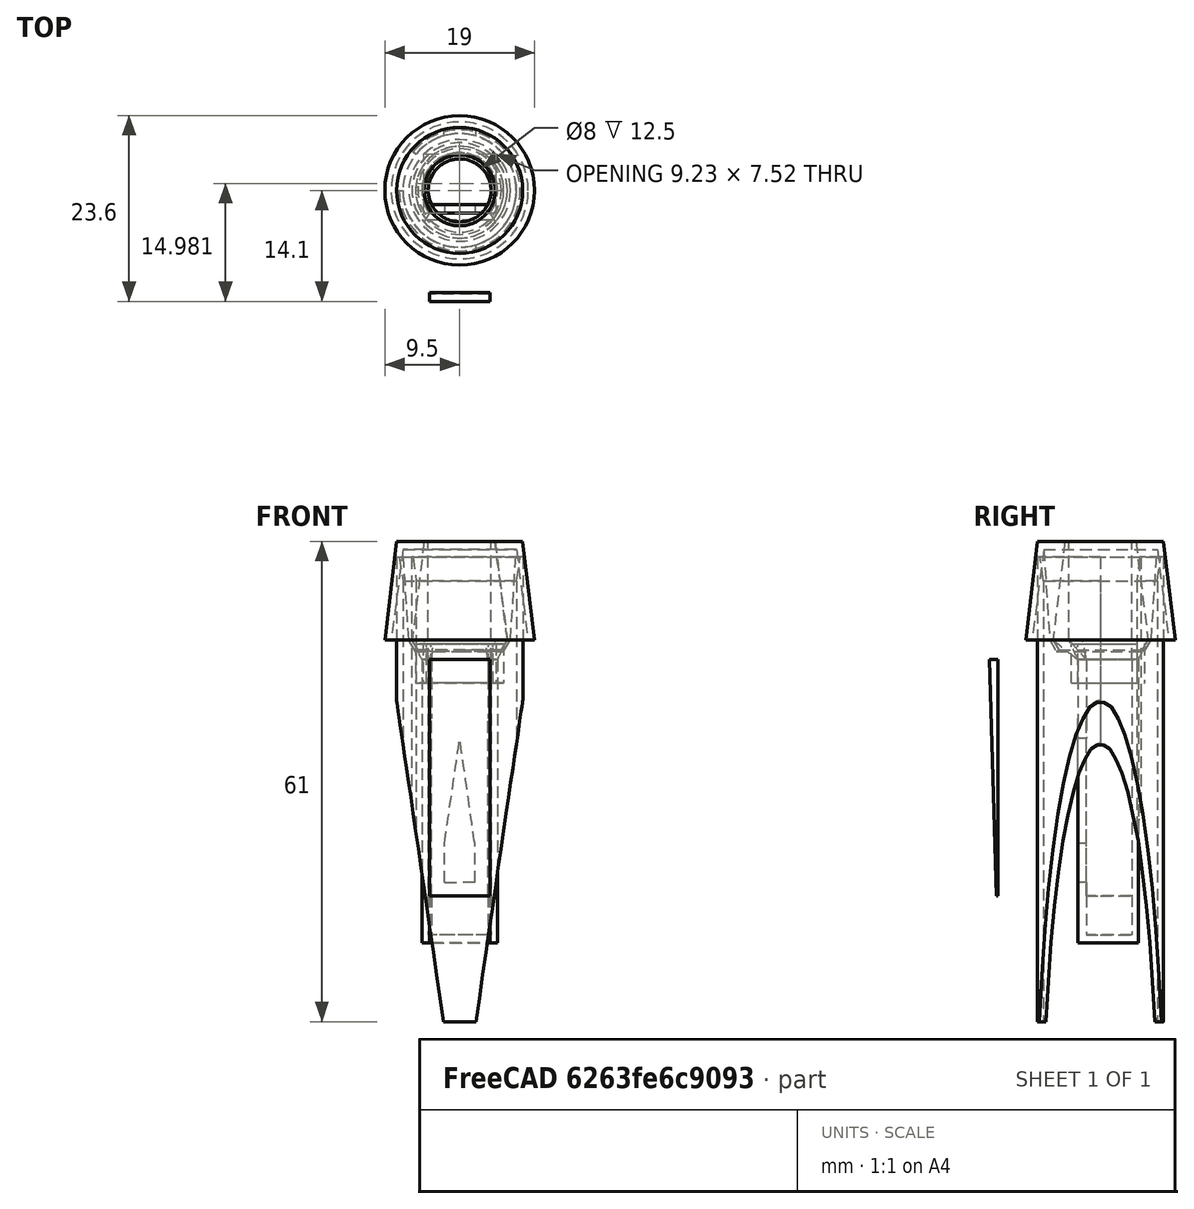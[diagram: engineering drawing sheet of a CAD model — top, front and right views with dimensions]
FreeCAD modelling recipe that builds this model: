
FCSTD DOCUMENT  (FreeCAD 1.1R44227 +647 (Git))
Label: stroik
License: All rights reserved
LicenseURL: https://en.wikipedia.org/wiki/All_rights_reserved
objects: Sketcher::SketchObject×15, PartDesign::Body×6, App::Point×6, PartDesign::Pocket×5, PartDesign::SubShapeBinder×5, PartDesign::Pad×4, PartDesign::AdditiveCylinder×2, PartDesign::Revolution×2, App::VarSet×1, PartDesign::Boolean×1, PartDesign::AdditiveLoft×1, Mesh::Feature×1
note: 85 computed .brp shape members not serialized (recipe doc carries the construction recipe); baked Part::Feature solids carry a one-line shape summary decoded from their .brp

FEATURE [App::VarSet] VarSet
  d_inner = 4
  d_outer = 4.8
  d_outer_plug = 6.05
  leaf_end_thickness = 0.2
  leaf_gap = 0
  leaf_len = 30
  leaf_start_thickness = 1.1
  plug_inner_start = 4
  plug_len = 15
  plug_outer_start = 4.5
FEATURE [PartDesign::AdditiveCylinder] Cylinder  label="HasCylinder"
  Angle = 360
  AttacherType = Attacher::AttachEngine3D
  FirstAngle = 0
  Height = 30
  Radius = 4.8
  Refine = true
  SecondAngle = 0
  Suppressed = false
  expr: Height = VarSet.leaf_len
  expr: Radius = VarSet.d_outer
FEATURE [Sketcher::SketchObject] Sketch
  ArcFitTolerance = 1e-06
  AttachmentSupport = -> [YZ_Plane]
  ExternalGeometry = -> [Cylinder]
  ExternalTypes = [0]
  FullyConstrained = true
  MakeInternals = false
  MapMode = 5
  Placement = pos=(0,0,0) rot=(0.57735,0.57735,0.57735;2.0944rad)
  _ExternalGeoVersion = 0
  expr: Constraints[12] = VarSet.leaf_gap + VarSet.d_outer / 2.5
  expr: Constraints[15] = VarSet.leaf_gap + VarSet.d_outer / 2 + 1 mm
  expr: Constraints[16] = VarSet.d_outer / 2.5
  expr: Constraints[19] = VarSet.leaf_len / 2 * 3 / 4
  expr: Constraints[1] = VarSet.leaf_len / 4
  expr: Constraints[25] = VarSet.leaf_gap / 3
  sketch-geometry (10):
    g0: LineSegment StartX=-2.88 StartY=30 StartZ=0 EndX=-2.88 EndY=22.5 EndZ=0
    g1: Circle [constr] CenterX=-2.88 CenterY=22.5 CenterZ=0 NormalX=0 NormalY=0 NormalZ=1 AngleXU=0 Radius=1
    g2: Circle [constr] CenterX=-2.88 CenterY=11.25 CenterZ=0 NormalX=0 NormalY=0 NormalZ=1 AngleXU=0 Radius=1
    g3: Circle [constr] CenterX=-2.88 CenterY=0 CenterZ=0 NormalX=0 NormalY=0 NormalZ=1 AngleXU=0 Radius=1
    g4: BSplineCurve PolesCount=3 KnotsCount=2 Degree=2 IsPeriodic=0
    g5: GeomPoint [constr] X=-2.88 Y=22.5 Z=0
    g6: GeomPoint [constr] X=-2.88 Y=0 Z=0
    g7: LineSegment StartX=-2.88 StartY=0 StartZ=0 EndX=-6.28 EndY=0 EndZ=0
    g8: LineSegment StartX=-6.28 StartY=30 StartZ=0 EndX=-2.88 EndY=30 EndZ=0
    g9: LineSegment StartX=-6.28 StartY=30 StartZ=0 EndX=-6.28 EndY=0 EndZ=0
  constraints (26):
    c: Vertical(g0)
    c: Distance(g0,g0) = 7.5
    c: Weight(g1) = 1
    c: Equal(g1,g2)
    c: Equal(g1,g3)
    c: InternalAlignment(g1,g4)
    c: InternalAlignment(g2,g4)
    c: InternalAlignment(g3,g4)
    c: InternalAlignment(g5,g4)
    c: InternalAlignment(g6,g4)
    c: Coincident(g1,g0)
    c: PointOnObject(g3,g-4)
    c: DistanceX(g-4,g4) = 1.92
    c: Coincident(g7,g4)
    c: Horizontal(g7)
    c: DistanceX(g7,g7) = 3.4
    c: DistanceX(g-3,g0) = 1.92
    c: Horizontal(g0,g-3)
    c: Vertical(g2,g0)
    c: DistanceY(g2,g0) = 11.25
    c: Coincident(g8,g0)
    c: Horizontal(g8)
    c: Coincident(g9,g8)
    c: Coincident(g9,g7)
    c: Vertical(g9)
    c: DistanceX(g4,g2) = 0
FEATURE [PartDesign::Pocket] Pocket  label="WithACut"
  BaseFeature = -> Cylinder
  Direction = (-1,0,0)
  Length = 5
  Length2 = 5
  Profile = -> Sketch
  ReferenceAxis = -> Sketch [N_Axis]
  Refine = true
  SideType = 2
  Suppressed = false
  Type = 1
  Type2 = 0
FEATURE [PartDesign::AdditiveCylinder] Cylinder001  label="HasCylinder001"
  Angle = 360
  AttacherType = Attacher::AttachEngine3D
  FirstAngle = 0
  Height = 30
  Radius = 4
  Refine = true
  SecondAngle = 0
  Suppressed = false
  expr: Height = VarSet.leaf_len
  expr: Radius = VarSet.d_inner
FEATURE [Sketcher::SketchObject] Sketch001
  ArcFitTolerance = 1e-06
  AttachmentSupport = -> [YZ_Plane001]
  ExternalGeometry = -> [Cylinder001]
  ExternalTypes = [0]
  FullyConstrained = true
  MakeInternals = false
  MapMode = 5
  Placement = pos=(0,0,0) rot=(0.57735,0.57735,0.57735;2.0944rad)
  _ExternalGeoVersion = 0
  expr: Constraints[12] = VarSet.leaf_gap + VarSet.d_inner / 2 + 0.2 mm
  expr: Constraints[15] = VarSet.leaf_gap + VarSet.d_inner / 2 + 1 mm
  expr: Constraints[16] = VarSet.d_inner / 2 + 0.2 mm
  expr: Constraints[19] = VarSet.leaf_len / 2 * 3 / 4
  expr: Constraints[1] = VarSet.leaf_len / 4
  sketch-geometry (10):
    g0: LineSegment StartX=-1.8 StartY=30 StartZ=0 EndX=-1.8 EndY=22.5 EndZ=0
    g1: Circle [constr] CenterX=-1.8 CenterY=22.5 CenterZ=0 NormalX=0 NormalY=0 NormalZ=1 AngleXU=0 Radius=1
    g2: Circle [constr] CenterX=-1.8 CenterY=11.25 CenterZ=0 NormalX=0 NormalY=0 NormalZ=1 AngleXU=0 Radius=1
    g3: Circle [constr] CenterX=-1.8 CenterY=0 CenterZ=0 NormalX=0 NormalY=0 NormalZ=1 AngleXU=0 Radius=1
    g4: BSplineCurve PolesCount=3 KnotsCount=2 Degree=2 IsPeriodic=0
    g5: GeomPoint [constr] X=-1.8 Y=22.5 Z=0
    g6: GeomPoint [constr] X=-1.8 Y=0 Z=0
    g7: LineSegment StartX=-1.8 StartY=0 StartZ=0 EndX=-4.8 EndY=0 EndZ=0
    g8: LineSegment StartX=-4.8 StartY=30 StartZ=0 EndX=-1.8 EndY=30 EndZ=0
    g9: LineSegment StartX=-4.8 StartY=30 StartZ=0 EndX=-4.8 EndY=0 EndZ=0
  constraints (25):
    c: Vertical(g0)
    c: Distance(g0,g0) = 7.5
    c: Weight(g1) = 1
    c: Equal(g1,g2)
    c: Equal(g1,g3)
    c: InternalAlignment(g1,g4)
    c: InternalAlignment(g2,g4)
    c: InternalAlignment(g3,g4)
    c: InternalAlignment(g5,g4)
    c: InternalAlignment(g6,g4)
    c: Coincident(g1,g0)
    c: PointOnObject(g3,g-4)
    c: DistanceX(g-4,g4) = 2.2
    c: Coincident(g7,g4)
    c: Horizontal(g7)
    c: DistanceX(g7,g7) = 3
    c: DistanceX(g-3,g0) = 2.2
    c: Horizontal(g0,g-3)
    c: Vertical(g2,g0)
    c: DistanceY(g2,g0) = 11.25
    c: Coincident(g8,g0)
    c: Horizontal(g8)
    c: Coincident(g9,g8)
    c: Coincident(g9,g7)
    c: Vertical(g9)
FEATURE [PartDesign::Pocket] Pocket001  label="WithACut001"
  BaseFeature = -> Cylinder001
  Direction = (-1,0,0)
  Length = 5
  Length2 = 5
  Profile = -> Sketch001
  ReferenceAxis = -> Sketch001 [N_Axis]
  Refine = true
  SideType = 2
  Suppressed = false
  Type = 1
  Type2 = 0
FEATURE [PartDesign::Body] Body001  label="SameShape"
  AllowCompound = false
  Group = -> [Cylinder001,Sketch001,Pocket001]
  Origin = -> Origin001
  Tip = -> Pocket001
FEATURE [PartDesign::Boolean] Boolean  label="Cut"
  BaseFeature = -> Pocket
  Group = -> [Body001]
  Refine = true
  Suppressed = false
  Type = 1
FEATURE [Sketcher::SketchObject] Sketch002
  ArcFitTolerance = 1e-06
  AttachmentSupport = -> [XZ_Plane]
  ExternalGeometry = -> [Boolean]
  ExternalTypes = [0]
  FullyConstrained = true
  MakeInternals = false
  MapMode = 5
  Placement = pos=(0,0,0) rot=(1,0,0;1.5708rad)
  _ExternalGeoVersion = 0
  sketch-geometry (19):
    g0: GeomPoint [constr] X=-2e-16 Y=26.625 Z=0
    g1: GeomPoint X=-1e-16 Y=13.3125 Z=0
    g2: GeomPoint X=0 Y=6.65625 Z=0
    g3: GeomPoint X=-1e-16 Y=19.9688 Z=0
    g4: GeomPoint X=0 Y=3.32812 Z=0
    g5: GeomPoint X=-4.21565 Y=13.3125 Z=0
    g6: GeomPoint X=4.21565 Y=13.3125 Z=0
    g7: GeomPoint X=-1.92 Y=1.66406 Z=0
    g8: GeomPoint X=1.92 Y=1.66406 Z=0
    g9: GeomPoint X=0 Y=1.66406 Z=0
    g10: GeomPoint X=-1.92 Y=1.66406 Z=0
    g11: GeomPoint X=1.92 Y=1.66406 Z=0
    g12: GeomPoint X=3.84 Y=1.66406 Z=0
    g13: GeomPoint X=-3.84 Y=1.66406 Z=0
    g14: LineSegment StartX=-1.92 StartY=1.66406 StartZ=0 EndX=1.92 EndY=1.66406 EndZ=0
    g15: LineSegment StartX=-1.92 StartY=1.66406 StartZ=0 EndX=-1.92 EndY=6.65625 EndZ=0
    g16: LineSegment StartX=-1e-16 StartY=19.9688 StartZ=0 EndX=1.92 EndY=6.65625 EndZ=0
    g17: LineSegment StartX=-1.92 StartY=6.65625 StartZ=0 EndX=-4e-16 EndY=19.9688 EndZ=0
    g18: LineSegment StartX=1.92 StartY=6.65625 StartZ=0 EndX=1.92 EndY=1.66406 EndZ=0
  constraints (28):
    c: Symmetric(g-5,g-5,g0)
    c: Symmetric(g0,g-1,g1)
    c: Symmetric(g0,g1,g3)
    c: Symmetric(g1,g-1,g2)
    c: Symmetric(g2,g-1,g4)
    c: Symmetric(g-5,g-6,g5)
    c: Symmetric(g-5,g-6,g6)
    c: Symmetric(g4,g-1,g9)
    c: Horizontal(g10,g9)
    c: Horizontal(g11,g9)
    c: PointOnObject(g12,g-4)
    c: PointOnObject(g13,g-3)
    c: Symmetric(g13,g9,g10)
    c: Symmetric(g12,g9,g11)
    c: Coincident(g14,g10)
    c: Coincident(g14,g11)
    c: Coincident(g15,g7)
    c: Coincident(g17,g3)
    c: Coincident(g16,g3)
    c: Coincident(g18,g8)
    c: Coincident(g10,g7)
    c: Coincident(g8,g11)
    c: Coincident(g15,g17)
    c: Coincident(g16,g18)
    c: Vertical(g8,g16)
    c: Horizontal(g16,g15)
    c: Vertical(g15,g7)
    c: Horizontal(g16,g2)
FEATURE [PartDesign::Pocket] Pocket002  label="HasHoleForTheAir"
  BaseFeature = -> Boolean
  Direction = (0,1,-2e-16)
  Length = 5
  Length2 = 5
  Profile = -> Sketch002
  ReferenceAxis = -> Sketch002 [N_Axis]
  Refine = true
  Reversed = true
  SideType = 0
  Suppressed = false
  Type = 1
  Type2 = 0
FEATURE [Sketcher::SketchObject] Sketch003
  ArcFitTolerance = 1e-06
  AttachmentSupport = -> [Pocket002]
  ExternalGeometry = -> [Pocket002]
  ExternalTypes = [0]
  FullyConstrained = true
  MakeInternals = false
  MapMode = 5
  Placement = pos=(0,0,0) rot=(1,0,0;3.14159rad)
  _ExternalGeoVersion = 0
FEATURE [PartDesign::Pad] Pad  label="HasExtensionAtTheEnd"
  BaseFeature = -> Pocket002
  Direction = (0,0,-1)
  Length = 5
  Length2 = 10
  Profile = -> Sketch003
  ReferenceAxis = -> Sketch003 [N_Axis]
  Refine = true
  SideType = 0
  Suppressed = false
  Type = 0
  Type2 = 0
FEATURE [Sketcher::SketchObject] Sketch004
  ArcFitTolerance = 1e-06
  AttachmentSupport = -> [Pad]
  ExternalGeometry = -> [Pad]
  ExternalTypes = [0,0,0]
  FullyConstrained = true
  MakeInternals = false
  MapMode = 5
  Placement = pos=(0,0,-5) rot=(1,0,0;3.14159rad)
  _ExternalGeoVersion = 0
FEATURE [PartDesign::Pad] Pad001  label="HasCap"
  BaseFeature = -> Pad
  Direction = (0,0,-1)
  Length = 1
  Length2 = 10
  Profile = -> Sketch004
  ReferenceAxis = -> Sketch004 [N_Axis]
  Refine = true
  SideType = 0
  Suppressed = false
  Type = 0
  Type2 = 0
FEATURE [Sketcher::SketchObject] Sketch005
  ArcFitTolerance = 1e-06
  AttachmentSupport = -> [Pad001]
  ExternalGeometry = -> [Pad001]
  ExternalTypes = [0]
  FullyConstrained = true
  MakeInternals = false
  MapMode = 5
  Placement = pos=(0,0,30) rot=(0,0,1;0rad)
  _ExternalGeoVersion = 0
  sketch-geometry (4):
    g0: LineSegment StartX=3.57211 StartY=-1.8 StartZ=0 EndX=-3.57211 EndY=-1.8 EndZ=0
    g1: LineSegment StartX=3.84 StartY=-2.88 StartZ=0 EndX=-3.84 EndY=-2.88 EndZ=0
    g2: ArcOfCircle CenterX=0 CenterY=0 CenterZ=0 NormalX=0 NormalY=0 NormalZ=1 AngleXU=0 Radius=4 StartAngle=5.81642 EndAngle=9.89154
    g3: ArcOfCircle CenterX=0 CenterY=0 CenterZ=0 NormalX=0 NormalY=0 NormalZ=1 AngleXU=0 Radius=4.8 StartAngle=5.63968 EndAngle=10.0683
  constraints (10):
    c: Coincident(g0,g-6)
    c: Horizontal(g0)
    c: Coincident(g1,g-7)
    c: Horizontal(g1)
    c: Coincident(g2,g-1)
    c: Coincident(g2,g0)
    c: Coincident(g2,g0)
    c: Coincident(g3,g2)
    c: Coincident(g3,g1)
    c: Coincident(g3,g1)
FEATURE [Sketcher::SketchObject] Sketch006
  ArcFitTolerance = 1e-06
  AttachmentOffset = pos=(0,0,2.5) rot=(0,0,1;0rad)
  AttachmentSupport = -> [Pad001]
  ExternalTypes = [0]
  FullyConstrained = true
  MakeInternals = false
  MapMode = 5
  Placement = pos=(0,0,32.5) rot=(0,0,1;0rad)
  _ExternalGeoVersion = 0
  expr: .AttachmentOffset.Base.x = 0 '
  expr: .AttachmentOffset.Base.z = VarSet.plug_len / 6
  expr: Constraints[2] = VarSet.d_inner * 2
  expr: Constraints[3] = VarSet.d_outer_plug * 2
  sketch-geometry (2):
    g0: Circle CenterX=0 CenterY=0 CenterZ=0 NormalX=0 NormalY=0 NormalZ=1 AngleXU=0 Radius=4
    g1: Circle CenterX=0 CenterY=0 CenterZ=0 NormalX=0 NormalY=0 NormalZ=1 AngleXU=0 Radius=6.05
  constraints (4):
    c: Coincident(g0,g-1)
    c: Coincident(g1,g0)
    c: Diameter(g0) = 8
    c: Diameter(g1) = 12.1
FEATURE [Sketcher::SketchObject] Sketch007
  ArcFitTolerance = 1e-06
  AttachmentOffset = pos=(0,0,15) rot=(0,0,1;0rad)
  AttachmentSupport = -> [Pad001]
  ExternalTypes = [0]
  FullyConstrained = true
  MakeInternals = false
  MapMode = 5
  Placement = pos=(0,0,45) rot=(0,0,1;0rad)
  _ExternalGeoVersion = 0
  expr: .AttachmentOffset.Base.z = VarSet.plug_len
  expr: Constraints[2] = VarSet.plug_inner_start * 2
  expr: Constraints[3] = VarSet.plug_outer_start * 2
  sketch-geometry (2):
    g0: Circle CenterX=0 CenterY=0 CenterZ=0 NormalX=0 NormalY=0 NormalZ=1 AngleXU=0 Radius=4
    g1: Circle CenterX=0 CenterY=0 CenterZ=0 NormalX=0 NormalY=0 NormalZ=1 AngleXU=0 Radius=4.5
  constraints (4):
    c: Coincident(g0,g-1)
    c: Coincident(g1,g0)
    c: Diameter(g0) = 8
    c: Diameter(g1) = 9
FEATURE [PartDesign::AdditiveLoft] AdditiveLoft  label="HasPlug"
  BaseFeature = -> Pad001
  Closed = false
  Profile = -> Sketch005
  Refine = true
  Ruled = true
  Sections = -> [Sketch006,Sketch007]
  Suppressed = false
FEATURE [PartDesign::Body] Body  label="MainPart"
  AllowCompound = false
  Group = -> [Cylinder,Sketch,Pocket,VarSet,Boolean,Sketch002,Pocket002,Sketch003,Pad,Sketch004,Pad001,Sketch005,Sketch006,Sketch007,AdditiveLoft]
  Origin = -> Origin
  Tip = -> AdditiveLoft
FEATURE [PartDesign::SubShapeBinder] Binder  label="Bases on MainPart"
  BindCopyOnChange = 0
  BindMode = 0
  ClaimChildren = false
  Context = -> Body002 [Binder.]
  Fuse = false
  MakeFace = true
  OffsetFill = false
  OffsetIntersection = false
  OffsetJoinType = 0
  OffsetOpenResult = false
  PartialLoad = false
  Refine = true
  Relative = true
  Support = -> [Body[Boolean.]]
  _Version = 2
FEATURE [Sketcher::SketchObject] Sketch009
  ArcFitTolerance = 1e-06
  AttachmentSupport = -> [XZ_Plane002]
  ExternalGeometry = -> [Binder]
  ExternalTypes = [0]
  FullyConstrained = true
  MakeInternals = false
  MapMode = 5
  Placement = pos=(0,0,0) rot=(1,0,0;1.5708rad)
  _ExternalGeoVersion = 0
  sketch-geometry (6):
    g0: LineSegment StartX=-3.84 StartY=30 StartZ=0 EndX=-3.84 EndY=22.5 EndZ=0
    g1: LineSegment StartX=-3.84 StartY=22.5 StartZ=0 EndX=-3.84 EndY=0 EndZ=0
    g2: LineSegment StartX=-3.84 StartY=0 StartZ=0 EndX=3.84 EndY=0 EndZ=0
    g3: LineSegment StartX=3.84 StartY=0 StartZ=0 EndX=3.84 EndY=22.5 EndZ=0
    g4: LineSegment StartX=3.84 StartY=22.5 StartZ=0 EndX=3.84 EndY=30 EndZ=0
    g5: LineSegment StartX=3.84 StartY=30 StartZ=0 EndX=-3.84 EndY=30 EndZ=0
  constraints (12):
    c: Coincident(g0,g-16)
    c: Coincident(g0,g-9)
    c: Coincident(g0,g1)
    c: Coincident(g1,g-18)
    c: Coincident(g1,g2)
    c: Coincident(g2,g-17)
    c: Coincident(g2,g3)
    c: Coincident(g3,g-4)
    c: Coincident(g3,g4)
    c: Coincident(g4,g-15)
    c: Coincident(g4,g5)
    c: Coincident(g5,g0)
FEATURE [PartDesign::Pad] Pad002  label="Has shape of the upper face"
  Direction = (0,-1,2e-16)
  Length = 10
  Length2 = 10
  Placement = pos=(0,0,0) rot=(1,0,0;1.5708rad)
  Profile = -> Sketch009
  ReferenceAxis = -> Sketch009 [N_Axis]
  Refine = true
  SideType = 0
  Suppressed = false
  Type = 0
  Type2 = 0
FEATURE [Sketcher::SketchObject] Sketch010
  ArcFitTolerance = 1e-06
  AttachmentSupport = -> [Pad002]
  ExternalGeometry = -> [Pad002]
  ExternalTypes = [0]
  FullyConstrained = true
  MakeInternals = false
  MapMode = 5
  Placement = pos=(3.84,0,0) rot=(0.707107,0,0.707107;3.14159rad)
  _ExternalGeoVersion = 0
  expr: Constraints[0] = VarSet.leaf_end_thickness
  expr: Constraints[9] = VarSet.leaf_start_thickness
  sketch-geometry (4):
    g0: LineSegment StartX=3.6e-15 StartY=0.2 StartZ=0 EndX=30 EndY=1.1 EndZ=0
    g1: LineSegment StartX=30 StartY=1.1 StartZ=0 EndX=30 EndY=10 EndZ=0
    g2: LineSegment StartX=3.6e-15 StartY=10 StartZ=0 EndX=3.6e-15 EndY=0.2 EndZ=0
    g3: LineSegment StartX=30 StartY=10 StartZ=0 EndX=3.6e-15 EndY=10 EndZ=0
  constraints (10):
    c: DistanceY(g-1,g0) = 0.2
    c: Coincident(g1,g0)
    c: Vertical(g1)
    c: Coincident(g2,g0)
    c: Vertical(g2)
    c: Coincident(g3,g1)
    c: Coincident(g3,g2)
    c: Coincident(g1,g-6)
    c: Coincident(g2,g-6)
    c: Distance(g0,g-5) = 1.1
FEATURE [PartDesign::Pocket] Pocket003  label="HasSteepShape"
  BaseFeature = -> Pad002
  Direction = (-1,0,2e-16)
  Length = 5
  Length2 = 5
  Placement = pos=(0,0,0) rot=(1,0,0;1.5708rad)
  Profile = -> Sketch010
  ReferenceAxis = -> Sketch010 [N_Axis]
  Refine = true
  SideType = 0
  Suppressed = false
  Type = 1
  Type2 = 0
FEATURE [PartDesign::Body] Body002  label="Leaf"
  AllowCompound = false
  Group = -> [Sketch009,Binder,Pad002,Sketch010,Pocket003]
  Origin = -> Origin002
  Placement = pos=(0,-13,0) rot=(0,0,1;0rad)
  Tip = -> Pocket003
FEATURE [PartDesign::SubShapeBinder] Binder001
  BindCopyOnChange = 0
  BindMode = 0
  ClaimChildren = false
  Context = -> Body003 [Binder001.]
  Fuse = false
  MakeFace = true
  OffsetFill = false
  OffsetIntersection = false
  OffsetJoinType = 0
  OffsetOpenResult = false
  PartialLoad = false
  Refine = true
  Relative = true
  Support = -> [Body[Pocket.]]
  _Version = 2
FEATURE [Sketcher::SketchObject] Sketch017
  ArcFitTolerance = 1e-06
  AttachmentSupport = -> [XY_Plane003]
  ExternalGeometry = -> [Binder001]
  ExternalTypes = [0]
  FullyConstrained = true
  MakeInternals = false
  MapMode = 5
  _ExternalGeoVersion = 0
  sketch-geometry (5):
    g0: LineSegment StartX=0 StartY=-2.88 StartZ=0 EndX=3.64 EndY=-2.88 EndZ=0
    g1: ArcOfCircle CenterX=0 CenterY=0 CenterZ=0 NormalX=0 NormalY=0 NormalZ=1 AngleXU=0 Radius=4.64155 StartAngle=5.61383 EndAngle=10.0941
    g2: LineSegment StartX=-4.22109 StartY=-3.68 StartZ=0 EndX=4.22109 EndY=-3.68 EndZ=0
    g3: ArcOfCircle CenterX=0 CenterY=0 CenterZ=0 NormalX=0 NormalY=0 NormalZ=1 AngleXU=0 Radius=5.6 StartAngle=5.56616 EndAngle=10.1418
    g4: LineSegment StartX=0 StartY=-2.88 StartZ=0 EndX=-3.64 EndY=-2.88 EndZ=0
  constraints (18):
    c: Coincident(g0,g-3)
    c: Coincident(g0,g-4)
    c: Coincident(g1,g-1)
    c: Coincident(g1,g0)
    c: Coincident(g0,g1)
    c: Horizontal(g0)
    c: Horizontal(g2)
    c: Coincident(g3,g1)
    c: Coincident(g3,g2)
    c: Coincident(g3,g2)
    c: Distance(g3,g-3) = 0.8
    c: Distance(g0,g2) = 0.8
    c: DistanceX(g0,g-4) = 0.2
    c: PointOnObject(g1,g0)
    c: Coincident(g4,g0)
    c: Coincident(g4,g1)
    c: Horizontal(g0,g-3)
    c: PointOnObject(g0,g-2)
FEATURE [PartDesign::Pad] Pad005
  Direction = (0,0,1)
  Length = 5
  Length2 = 10
  Profile = -> Sketch017
  ReferenceAxis = -> Sketch017 [N_Axis]
  Refine = true
  SideType = 0
  Suppressed = false
  Type = 0
  Type2 = 0
FEATURE [PartDesign::Body] Body003  label="Ring"
  AllowCompound = false
  Group = -> [Binder001,Sketch017,Pad005]
  Origin = -> Origin003
  Placement = pos=(0,0,27) rot=(0,0,1;0rad)
  Tip = -> Pad005
FEATURE [PartDesign::SubShapeBinder] Binder002
  BindCopyOnChange = 0
  BindMode = 0
  ClaimChildren = false
  Context = -> Body004 [Binder002.]
  Fuse = false
  MakeFace = true
  OffsetFill = false
  OffsetIntersection = false
  OffsetJoinType = 0
  OffsetOpenResult = false
  PartialLoad = false
  Refine = true
  Relative = true
  Support = -> [Body[AdditiveLoft.]]
  _Version = 2
FEATURE [Sketcher::SketchObject] Sketch018
  ArcFitTolerance = 1e-06
  AttachmentSupport = -> [YZ_Plane004]
  ExternalGeometry = -> [Binder002]
  ExternalTypes = [0]
  FullyConstrained = false
  MakeInternals = false
  MapMode = 5
  Placement = pos=(0,0,0) rot=(0.57735,0.57735,0.57735;2.0944rad)
  _ExternalGeoVersion = 0
  sketch-geometry (10):
    g0: GeomPoint X=-1e-16 Y=45 Z=0
    g1: LineSegment StartX=-4.5 StartY=45 StartZ=0 EndX=-8 EndY=45 EndZ=0
    g2: LineSegment StartX=-4.5 StartY=45 StartZ=0 EndX=-6.05 EndY=32.5 EndZ=0
    g3: LineSegment StartX=-7.2 StartY=44 StartZ=0 EndX=-6.45 EndY=32.5 EndZ=0
    g4: LineSegment StartX=-8 StartY=45 StartZ=0 EndX=-9.5 EndY=32.5 EndZ=0
    g5: LineSegment StartX=-7.2 StartY=44 StartZ=0 EndX=-8.7 EndY=32.5 EndZ=0
    g6: LineSegment StartX=-8.7 StartY=32.5 StartZ=0 EndX=-9.5 EndY=32.5 EndZ=0
    g7: LineSegment StartX=-6.45 StartY=32.5 StartZ=0 EndX=-5.6 EndY=31.0278 EndZ=0
    g8: LineSegment StartX=-6.05 StartY=32.5 StartZ=0 EndX=-5.3 EndY=31.201 EndZ=0
    g9: LineSegment StartX=-5.6 StartY=31.0278 StartZ=0 EndX=-5.3 EndY=31.201 EndZ=0
  constraints (26):
    c: Horizontal(g1)
    c: Distance(g1,g-2) = 8
    c: Coincident(g2,g1)
    c: Horizontal(g3,g-4)
    c: DistanceY(g3,g1) = 1
    c: Coincident(g4,g1)
    c: Coincident(g5,g3)
    c: Coincident(g6,g4)
    c: Horizontal(g4,g5)
    c: Coincident(g5,g6)
    c: DistanceX(g6,g6) = 0.8
    c: DistanceX(g1,g3) = 0.8
    c: DistanceX(g4,g1) = 1.5
    c: Horizontal(g5,g2)
    c: Coincident(g2,g-4)
    c: Horizontal(g3,g2)
    c: DistanceX(g3,g2) = 0.4
    c: Coincident(g7,g3)
    c: Coincident(g8,g2)
    c: Coincident(g9,g7)
    c: Coincident(g9,g8)
    c: Angle(g8,g9) = 1.5708
    c: Angle(g9,g7) = 1.5708
    c: Distance(g8,g8) = 1.5
    c: Coincident(g-5,g1)
    c: Angle(g8) = -1.0472
FEATURE [PartDesign::Revolution] Revolution
  Angle = 360
  Angle2 = 60
  Axis = (0,0,1)
  Base = (0,0,0)
  FuseOrder = 1
  Placement = pos=(0,0,0) rot=(1,1,1;2.0944rad)
  Profile = -> Sketch018
  ReferenceAxis = -> Sketch018 [V_Axis]
  Refine = true
  Suppressed = false
  Type = 0
FEATURE [PartDesign::Body] Body004  label="Socket"
  AllowCompound = false
  Group = -> [Binder002,Sketch018,Revolution]
  Origin = -> Origin004
  Tip = -> Revolution
FEATURE [App::Point] Origin005  label="Origin"
  Role = Origin
FEATURE [App::Point] Origin006  label="Origin"
  Role = Origin
FEATURE [App::Point] Origin007  label="Origin"
  Role = Origin
FEATURE [App::Point] Origin008  label="Origin"
  Role = Origin
FEATURE [App::Point] Origin009  label="Origin"
  Role = Origin
FEATURE [App::Point] Origin011
  Role = Origin
FEATURE [PartDesign::SubShapeBinder] Binder003
  BindCopyOnChange = 0
  BindMode = 0
  ClaimChildren = false
  Context = -> Body005 [Binder003.]
  Fuse = false
  MakeFace = true
  OffsetFill = false
  OffsetIntersection = false
  OffsetJoinType = 0
  OffsetOpenResult = false
  PartialLoad = false
  Refine = true
  Relative = true
  Support = -> [Body]
  _Version = 2
FEATURE [PartDesign::SubShapeBinder] Binder004
  BindCopyOnChange = 0
  BindMode = 0
  ClaimChildren = false
  Context = -> Body005 [Binder004.]
  Fuse = false
  MakeFace = true
  OffsetFill = false
  OffsetIntersection = false
  OffsetJoinType = 0
  OffsetOpenResult = false
  PartialLoad = false
  Refine = true
  Relative = true
  Support = -> [Body004]
  _Version = 2
FEATURE [Sketcher::SketchObject] Sketch019
  ArcFitTolerance = 1e-06
  AttachmentSupport = -> [Origin010]
  ExternalGeometry = -> [Binder004,Binder003]
  ExternalTypes = [0,0,0]
  FullyConstrained = true
  MakeInternals = false
  MapMode = 5
  Placement = pos=(0,0,0) rot=(1,0,0;1.5708rad)
  _ExternalGeoVersion = 1
  sketch-geometry (6):
    g0: LineSegment StartX=-8.02 StartY=43.0001 StartZ=0 EndX=-8.02 EndY=-16 EndZ=0
    g1: LineSegment [constr] StartX=-8 StartY=45 StartZ=0 EndX=-6.05 EndY=32.5 EndZ=0
    g2: LineSegment StartX=-8.02 StartY=43.0001 StartZ=0 EndX=-7.68802 EndY=43.0001 EndZ=0
    g3: LineSegment StartX=-7.68802 StartY=43.0001 StartZ=0 EndX=-7.22 EndY=40 EndZ=0
    g4: LineSegment StartX=-7.22 StartY=40 StartZ=0 EndX=-7.22 EndY=-16 EndZ=0
    g5: LineSegment StartX=-7.22 StartY=-16 StartZ=0 EndX=-8.02 EndY=-16 EndZ=0
  constraints (17):
    c: Vertical(g0)
    c: DistanceY(g0,g-4) = 10
    c: Distance(g0,g-3) = 2
    c: Coincident(g1,g-5)
    c: Coincident(g2,g0)
    c: PointOnObject(g2,g1)
    c: Horizontal(g2)
    c: Coincident(g3,g2)
    c: PointOnObject(g3,g1)
    c: Coincident(g4,g3)
    c: Vertical(g4)
    c: Coincident(g5,g0)
    c: Coincident(g4,g5)
    c: Horizontal(g5)
    c: DistanceX(g0,g3) = 0.8
    c: DistanceX(g0,g1) = 0.02
    c: Coincident(g-3,g1)
FEATURE [PartDesign::Revolution] Revolution001
  Angle = 320
  Angle2 = 0
  Axis = (0,2e-16,1)
  Base = (0,0,0)
  FuseOrder = 0
  Profile = -> Sketch019
  ReferenceAxis = -> Sketch019 [V_Axis]
  Refine = true
  Suppressed = false
  Type = 0
FEATURE [Sketcher::SketchObject] Sketch020
  ArcFitTolerance = 1e-06
  AttachmentSupport = -> [Origin010]
  ExternalTypes = [0]
  FullyConstrained = false
  MakeInternals = false
  MapMode = 5
  Placement = pos=(0,0,0) rot=(1,0,0;1.5708rad)
  _ExternalGeoVersion = 1
  sketch-geometry (6):
    g0: LineSegment StartX=-11.7655 StartY=50.5377 StartZ=0 EndX=0 EndY=-30.0739 EndZ=0
    g1: LineSegment StartX=11.7655 StartY=50.5377 StartZ=0 EndX=0 EndY=-30.0739 EndZ=0
    g2: LineSegment StartX=11.7655 StartY=50.5377 StartZ=0 EndX=11.7655 EndY=-23.2607 EndZ=0
    g3: LineSegment StartX=0 StartY=-30.0739 StartZ=0 EndX=11.7655 EndY=-23.2607 EndZ=0
    g4: LineSegment StartX=0 StartY=-30.0739 StartZ=0 EndX=-11.7655 EndY=-23.2607 EndZ=0
    g5: LineSegment StartX=-11.7655 StartY=50.5377 StartZ=0 EndX=-11.7655 EndY=-23.2607 EndZ=0
  constraints (11):
    c: PointOnObject(g0,g-2)
    c: Coincident(g1,g0)
    c: Coincident(g2,g1)
    c: Coincident(g3,g0)
    c: Coincident(g3,g2)
    c: Coincident(g4,g0)
    c: Coincident(g5,g0)
    c: Coincident(g5,g4)
    c: Vertical(g5)
    c: Symmetric(g1,g0,g-2)
    c: Symmetric(g2,g4,g-2)
FEATURE [PartDesign::Pocket] Pocket004
  BaseFeature = -> Revolution001
  Direction = (0,1,-2e-16)
  Length = 5
  Length2 = 5
  Profile = -> Sketch020
  ReferenceAxis = -> Sketch020 [N_Axis]
  Refine = true
  SideType = 2
  Suppressed = false
  Type = 1
  Type2 = 0
FEATURE [Sketcher::SketchObject] Sketch021
  ArcFitTolerance = 1e-06
  AttachmentSupport = -> [Origin010]
  ExternalTypes = [0]
  FullyConstrained = true
  MakeInternals = false
  MapMode = 5
  Placement = pos=(0,0,0) rot=(1,0,0;1.5708rad)
  _ExternalGeoVersion = 1
FEATURE [PartDesign::Body] Body005  label="SocketFixer"
  AllowCompound = true
  Group = -> [Binder003,Binder004,Sketch019,Revolution001,Sketch020,Pocket004,Sketch021]
  Origin = -> Origin010
  Tip = -> Pocket004
FEATURE [Mesh::Feature] Mesh  label="Socket (Meshed)"
